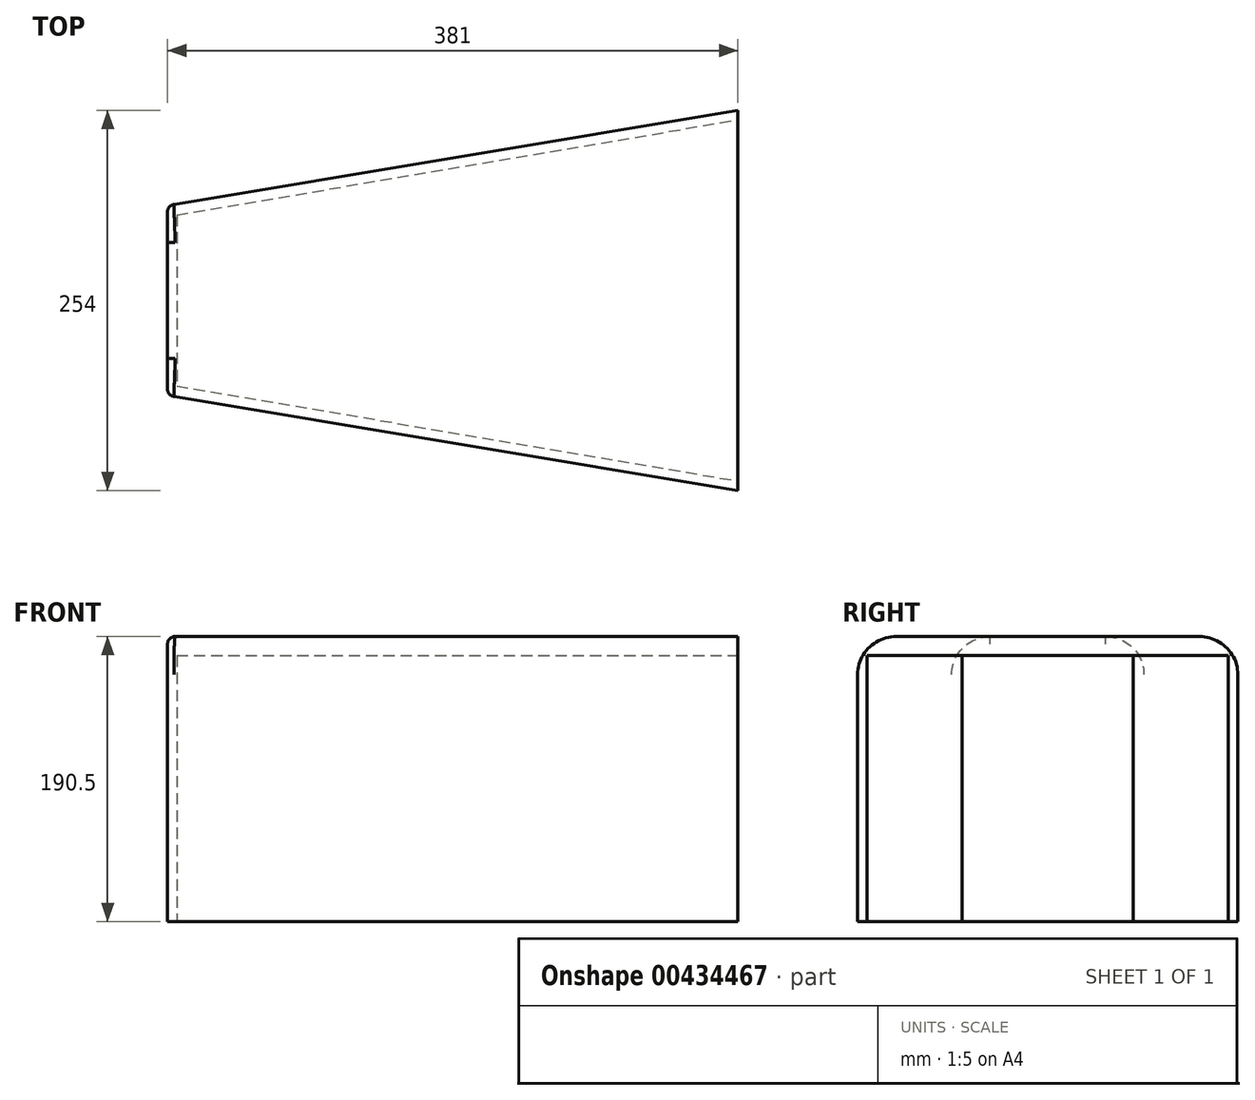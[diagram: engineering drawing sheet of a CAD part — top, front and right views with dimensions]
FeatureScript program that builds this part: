
annotation { "Feature Type Name" : "Feature", "Feature Type Description" : "" }
export const myFeature = defineFeature(function(context is Context, id is Id, definition is map)
    precondition{}
    {
        {
            var Q0;
            Q0=qCreatedBy(makeId("Top.planeOp"),FACE);
            var sketch = newSketch(context, id + "F0", { "sketchPlane" : qUnion([Q0])});
            skLineSegment(sketch, "E0", {"start": v(0, 127) * mm, "end": v(0, -127) * mm});
            skLineSegment(sketch, "E1", {"start": v(0, 0) * mm, "end": v(-381, 0) * mm});
            skLineSegment(sketch, "E2", {"start": v(-381, 0) * mm, "end": v(-381, 63.5) * mm});
            skLineSegment(sketch, "E3", {"start": v(-381, 0) * mm, "end": v(-381, -63.5) * mm});
            skLineSegment(sketch, "E4", {"start": v(-381, -63.5) * mm, "end": v(0, -127) * mm});
            skLineSegment(sketch, "E5", {"start": v(-381, 63.5) * mm, "end": v(0, 127) * mm});
            skSolve(sketch);
        }
        {
            var Q0;
            Q0 = qSketchRegion(id + "F0", true);
            extrude(context, id + "F1", {"entities" : qUnion([Q0]), "depth" : 190.5 * mm});
        }
        {
            var Q0;
            Q0=makeQuery(id+"F1.opExtrude","CAP_EDGE",EDGE,{"disambiguationData":[OSD([sQuery(id+"F0.wireOp",EDGE,"E4")])],"isStart":false});
            var Q1;
            Q1=makeQuery(id+"F1.opExtrude","CAP_EDGE",EDGE,{"disambiguationData":[OSD([sQuery(id+"F0.wireOp",EDGE,"E5")])],"isStart":false});
            fillet(context, id + "F2", {"entities" : qUnion([Q0, Q1]), "radius" : 25.4 * mm, "tangentPropagation" : true, "allowEdgeOverflow" : false});
        }
        {
            var Q0;
            Q0=makeQuery(id+"F1.opExtrude","CAP_EDGE",EDGE,{"disambiguationData":[OSD([sQuery(id+"F0.wireOp",EDGE,"E2"),sQuery(id+"F0.wireOp",EDGE,"E3")])],"isStart":false});
            fillet(context, id + "F3", {"entities" : qUnion([Q0]), "radius" : 5.08 * mm, "tangentPropagation" : true, "allowEdgeOverflow" : false});
        }
        {
            var Q0;
            Q0=qCreatedBy(makeId("Top.planeOp"),FACE);
            var sketch = newSketch(context, id + "F4", { "sketchPlane" : qUnion([Q0])});
            skLineSegment(sketch, "E6", {"start": v(0, -120.65) * mm, "end": v(0, 120.65) * mm});
            skLineSegment(sketch, "E7", {"start": v(-381.18, 0) * mm, "end": v(-374.83, 0) * mm});
            skLineSegment(sketch, "E8", {"start": v(-374.83, 0) * mm, "end": v(-374.83, -57.15) * mm});
            skLineSegment(sketch, "E9", {"start": v(-374.83, 0) * mm, "end": v(-374.83, 57.15) * mm});
            skLineSegment(sketch, "E10", {"start": v(-374.83, -57.15) * mm, "end": v(0, -120.65) * mm});
            skLineSegment(sketch, "E11", {"start": v(-374.83, 57.15) * mm, "end": v(0, 120.65) * mm});
            skSolve(sketch);
        }
        {
            var Q0;
            Q0 = qSketchRegion(id + "F4", true);
            extrude(context, id + "F5", {"entities" : qUnion([Q0]), "operationType" : NewBodyOperationType.REMOVE, "depth" : 177.8 * mm});
        }
    });
